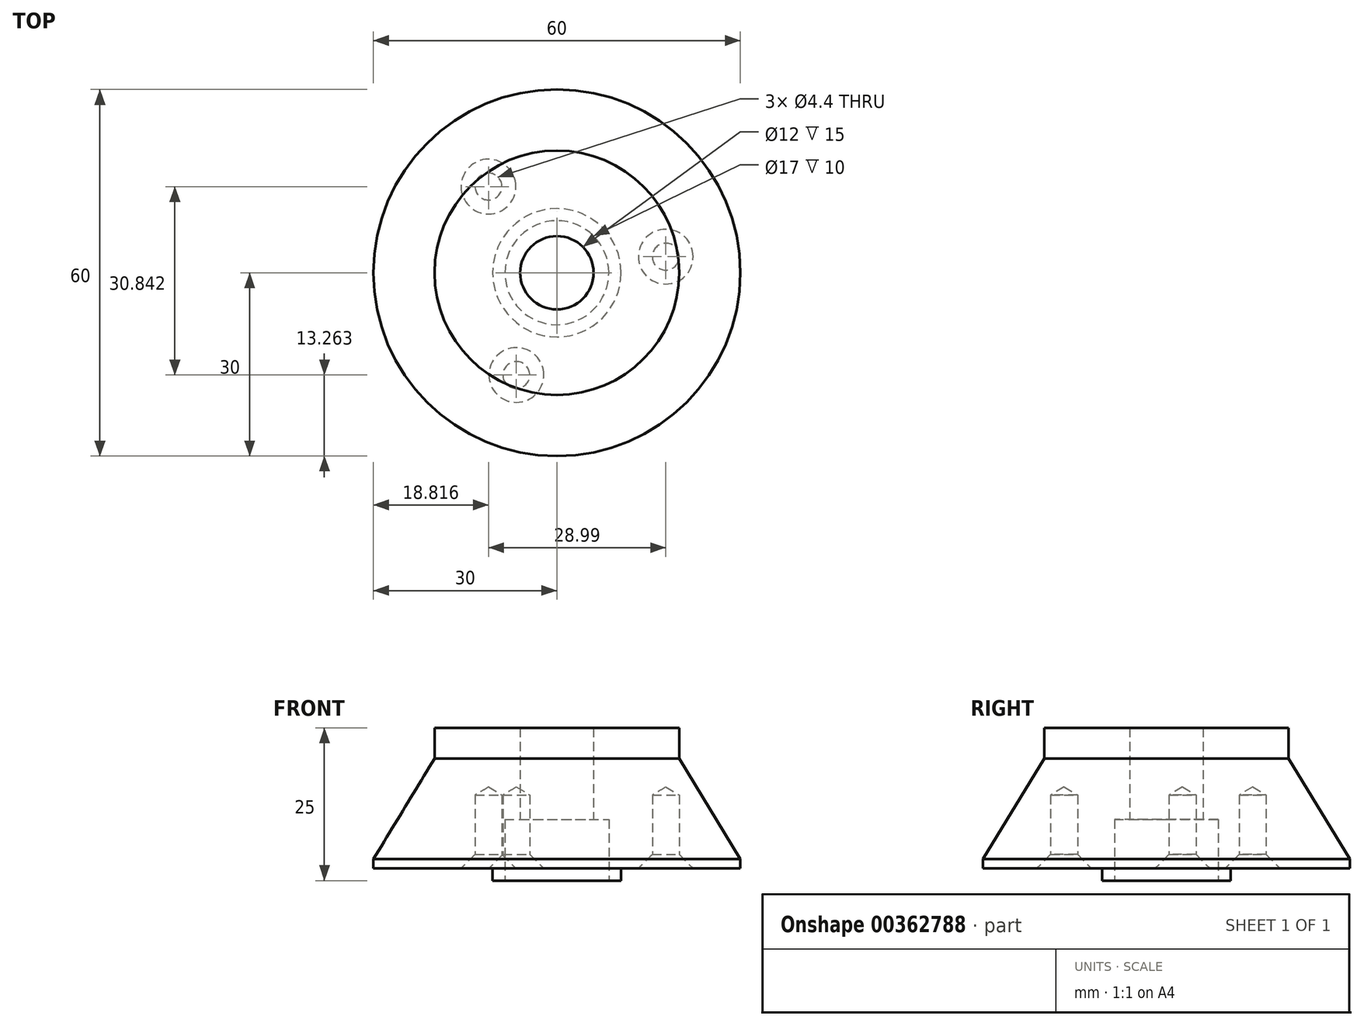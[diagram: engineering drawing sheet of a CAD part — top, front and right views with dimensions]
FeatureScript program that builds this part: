
annotation { "Feature Type Name" : "Feature", "Feature Type Description" : "" }
export const myFeature = defineFeature(function(context is Context, id is Id, definition is map)
    precondition{}
    {
        {
            var Q0;
            Q0=qCreatedBy(makeId("Front.planeOp"),FACE);
            var sketch = newSketch(context, id + "F0", { "sketchPlane" : qUnion([Q0])});
            skLineSegment(sketch, "E0", {"start": v(6, 25) * mm, "end": v(20, 25) * mm});
            skLineSegment(sketch, "E1", {"start": v(20, 25) * mm, "end": v(20, 20) * mm});
            skLineSegment(sketch, "E2", {"start": v(20, 20) * mm, "end": v(30, 3.5) * mm});
            skLineSegment(sketch, "E3", {"start": v(30, 3.5) * mm, "end": v(30, 2) * mm});
            skLineSegment(sketch, "E4", {"start": v(30, 2) * mm, "end": v(10.5, 2) * mm});
            skLineSegment(sketch, "E5", {"start": v(10.5, 2) * mm, "end": v(10.5, 0) * mm});
            skLineSegment(sketch, "E6", {"start": v(10.5, 0) * mm, "end": v(8.5, 0) * mm});
            skLineSegment(sketch, "E7", {"start": v(8.5, 0) * mm, "end": v(8.5, 10) * mm});
            skLineSegment(sketch, "E8", {"start": v(8.5, 10) * mm, "end": v(6, 10) * mm});
            skLineSegment(sketch, "E9", {"start": v(6, 10) * mm, "end": v(6, 25) * mm});
            skLineSegment(sketch, "E10", {"start": v(0, 0) * mm, "end": v(0, 33.96) * mm, "construction": true});
            skSolve(sketch);
        }
        {
            var Q0;
            Q0=makeQuery(id+"F0.imprint","IMPRINT",FACE,{"disambiguationData":[TD([[makeQuery(id+"F0.imprint","IMPRINT",EDGE,{"derivedFrom":sQuery(id+"F0.wireOp",EDGE,"E0")}),-1.0]])]});
            var Q1;
            Q1=sQuery(id+"F0.wireOp",EDGE,"E10");
            revolve(context, id + "F1", {"entities" : qUnion([Q0]), "axis" : qUnion([Q1]), "revolveType" : RevolveType.FULL});
        }
        {
            var Q0;
            Q0=makeQuery(id+"F1.opRevolve","SWEPT_FACE",FACE,{"disambiguationData":[OSD([sQuery(id+"F0.wireOp",EDGE,"E4")])]});
            var sketch = newSketch(context, id + "F2", { "sketchPlane" : qUnion([Q0])});
            skPoint(sketch, "E11", {"position": v(-6.62, 16.74) * mm});
            skLineSegment(sketch, "E12", {"start": v(0, 0) * mm, "end": v(-6.62, 16.74) * mm, "construction": true});
            skPoint(sketch, "E13.1.0", {"position": v(-11.18, -14.1) * mm});
            skPoint(sketch, "E13.2.0", {"position": v(17.8, -2.63) * mm});
            skPoint(sketch, "E13.center", {"position": v(0, 0) * mm});
            skSolve(sketch);
        }
        {
            var Q0;
            Q0=sQuery(id+"F2.wireOp",VERTEX,"E11");
            var Q1;
            Q1=sQuery(id+"F2.wireOp",VERTEX,"E13.1.0");
            var Q2;
            Q2=sQuery(id+"F2.wireOp",VERTEX,"E13.2.0");
            var Q3;
            Q3=makeQuery(id+"F1.opRevolve","SWEPT_BODY",BODY,{"disambiguationData":[OSD([sQuery(id+"F0.wireOp",EDGE,"E0"),sQuery(id+"F0.wireOp",EDGE,"E1"),sQuery(id+"F0.wireOp",EDGE,"E2"),sQuery(id+"F0.wireOp",EDGE,"E3"),sQuery(id+"F0.wireOp",EDGE,"E4"),sQuery(id+"F0.wireOp",EDGE,"E5"),sQuery(id+"F0.wireOp",EDGE,"E6"),sQuery(id+"F0.wireOp",EDGE,"E7"),sQuery(id+"F0.wireOp",EDGE,"E8"),sQuery(id+"F0.wireOp",EDGE,"E9")])]});
            hole(context, id + "F3", {"style" : HoleStyle.C_SINK, "endStyle" : HoleEndStyle.BLIND, "standardTappedOrClearance" : lookupTablePath({ "standard" : "ISO", "fit" : "Normal", "size" : "M4", "type" : "Clearance" }), "standardBlindInLast" : lookupTablePath({ "fit" : "Standard", "standard" : "ISO", "size" : "M4", "type" : "Clearance" }), "holeDiameter" : 4.4 * mm, "cSinkDiameter" : 8.96 * mm, "cSinkAngle" : 90 * degree, "holeDepth" : 12 * mm, "isTappedThrough" : true, "tappedDepth" : 12 * mm, "tapClearance" : 3, "locations" : qUnion([Q0, Q1, Q2]), "scope" : qUnion([Q3])});
        }
    });
